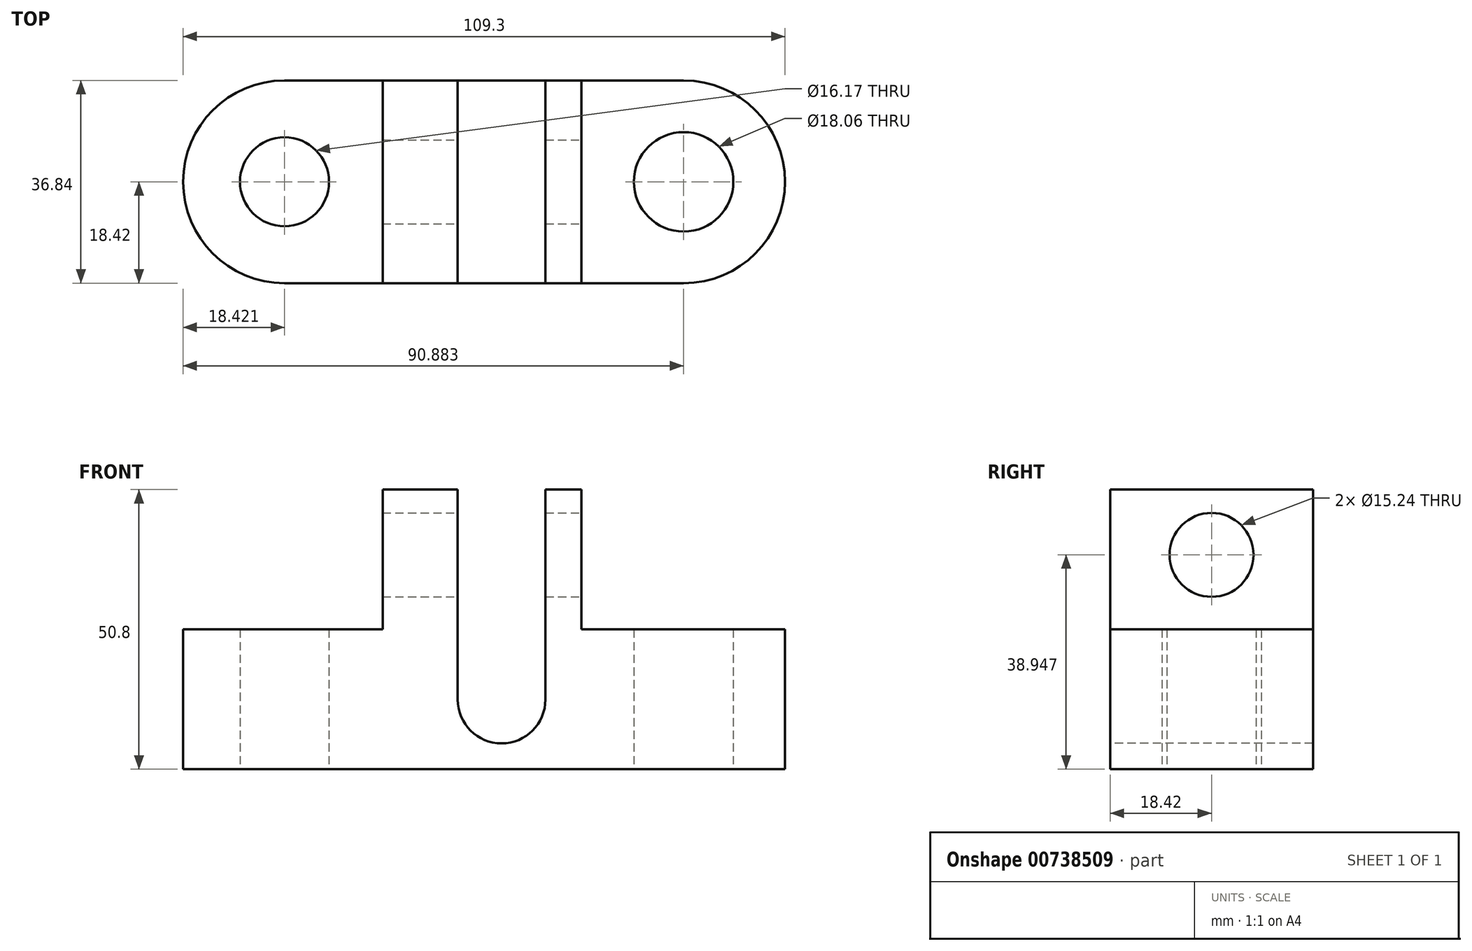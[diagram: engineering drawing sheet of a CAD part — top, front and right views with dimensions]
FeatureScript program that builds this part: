
annotation { "Feature Type Name" : "Feature", "Feature Type Description" : "" }
export const myFeature = defineFeature(function(context is Context, id is Id, definition is map)
    precondition{}
    {
        {
            var Q0;
            Q0=qCreatedBy(makeId("Top.planeOp"),FACE);
            var sketch = newSketch(context, id + "F0", { "sketchPlane" : qUnion([Q0])});
            skArc(sketch, "E0", {"start": v(-39.4, 18.42) * mm, "mid": v(-57.83, 0) * mm, "end": v(-39.4, -18.42) * mm});
            skArc(sketch, "E1", {"start": v(33.05, -18.42) * mm, "mid": v(51.47, 0) * mm, "end": v(33.05, 18.42) * mm});
            skLineSegment(sketch, "E2", {"start": v(-39.4, 18.42) * mm, "end": v(33.05, 18.42) * mm});
            skLineSegment(sketch, "E3", {"start": v(-39.4, -18.42) * mm, "end": v(33.05, -18.42) * mm});
            skCircle(sketch, "E4", {"center": v(-39.4, 0) * mm, "radius": 8.08 * mm});
            skCircle(sketch, "E5", {"center": v(33.05, 0) * mm, "radius": 9.03 * mm});
            skSolve(sketch);
        }
        {
            var Q0;
            Q0=makeQuery(id+"F0.imprint","IMPRINT",FACE,{"disambiguationData":[TD([[makeQuery(id+"F0.imprint","IMPRINT",EDGE,{"derivedFrom":sQuery(id+"F0.wireOp",EDGE,"E0")}),1.0]])]});
            extrude(context, id + "F1", {"entities" : qUnion([Q0]), "depth" : 25.4 * mm, "offsetDistance" : 25.4 * mm});
        }
        {
            var Q0;
            Q0=makeQuery(id+"F1.opExtrude","CAP_FACE",FACE,{"disambiguationData":[OSD([sQuery(id+"F0.wireOp",EDGE,"E0"),sQuery(id+"F0.wireOp",EDGE,"E1"),sQuery(id+"F0.wireOp",EDGE,"E2"),sQuery(id+"F0.wireOp",EDGE,"E3"),sQuery(id+"F0.wireOp",EDGE,"E4"),sQuery(id+"F0.wireOp",EDGE,"E5")])],"isStart":false});
            var sketch = newSketch(context, id + "F2", { "sketchPlane" : qUnion([Q0])});
            skLineSegment(sketch, "E6.bottom", {"start": v(-21.6, -18.42) * mm, "end": v(14.48, -18.42) * mm});
            skLineSegment(sketch, "E6.top", {"start": v(-21.6, 18.42) * mm, "end": v(14.48, 18.42) * mm});
            skLineSegment(sketch, "E6.left", {"start": v(-21.6, -18.42) * mm, "end": v(-21.6, 18.42) * mm});
            skLineSegment(sketch, "E6.right", {"start": v(14.48, -18.42) * mm, "end": v(14.48, 18.42) * mm});
            skSolve(sketch);
        }
        {
            var Q0;
            Q0=makeQuery(id+"F2.imprint","IMPRINT",FACE,{"disambiguationData":[TD([[makeQuery(id+"F2.imprint","IMPRINT",EDGE,{"derivedFrom":sQuery(id+"F2.wireOp",EDGE,"E6.bottom")}),1.0]])]});
            extrude(context, id + "F3", {"entities" : qUnion([Q0]), "operationType" : NewBodyOperationType.ADD, "depth" : 25.4 * mm, "offsetDistance" : 25.4 * mm});
        }
        {
            var Q0;
            Q0=makeQuery(id+"F3.boolean.opBoolean","MERGE",FACE,{"derivedFrom":[makeQuery(id+"F1.opExtrude","SWEPT_FACE",FACE,{"disambiguationData":[OSD([sQuery(id+"F0.wireOp",EDGE,"E3")])]}),makeQuery(id+"F3.opExtrude","SWEPT_FACE",FACE,{"disambiguationData":[OSD([sQuery(id+"F2.wireOp",EDGE,"E6.bottom")])]})]});
            var sketch = newSketch(context, id + "F4", { "sketchPlane" : qUnion([Q0])});
            skArc(sketch, "E7", {"start": v(-7.96, 12.65) * mm, "mid": v(0, 4.7) * mm, "end": v(7.96, 12.65) * mm});
            skLineSegment(sketch, "E8", {"start": v(-7.96, 12.65) * mm, "end": v(-7.96, 50.8) * mm});
            skLineSegment(sketch, "E9", {"start": v(7.96, 12.65) * mm, "end": v(7.96, 50.8) * mm});
            skLineSegment(sketch, "E10", {"start": v(-7.96, 50.8) * mm, "end": v(7.96, 50.8) * mm});
            skSolve(sketch);
        }
        {
            var Q0;
            Q0=makeQuery(id+"F4.imprint","IMPRINT",FACE,{"disambiguationData":[TD([[makeQuery(id+"F4.imprint","IMPRINT",EDGE,{"derivedFrom":sQuery(id+"F4.wireOp",EDGE,"E7")}),1.0]])]});
            extrude(context, id + "F5", {"entities" : qUnion([Q0]), "operationType" : NewBodyOperationType.REMOVE, "endBound" : BoundingType.THROUGH_ALL, "oppositeDirection" : true, "depth" : 25.4 * mm, "offsetDistance" : 25.4 * mm});
        }
        {
            var Q0;
            Q0=makeQuery(id+"F3.opExtrude","SWEPT_FACE",FACE,{"disambiguationData":[OSD([sQuery(id+"F2.wireOp",EDGE,"E6.right")])]});
            var sketch = newSketch(context, id + "F6", { "sketchPlane" : qUnion([Q0])});
            skCircle(sketch, "E11", {"center": v(0, 38.95) * mm, "radius": 7.62 * mm});
            skSolve(sketch);
        }
        {
            var Q0;
            Q0=makeQuery(id+"F6.imprint","IMPRINT",FACE,{"disambiguationData":[TD([[makeQuery(id+"F6.imprint","IMPRINT",EDGE,{"derivedFrom":sQuery(id+"F6.wireOp",EDGE,"E11")}),1.0]])]});
            extrude(context, id + "F7", {"entities" : qUnion([Q0]), "operationType" : NewBodyOperationType.REMOVE, "endBound" : BoundingType.THROUGH_ALL, "oppositeDirection" : true, "depth" : 25.4 * mm, "offsetDistance" : 25.4 * mm});
        }
    });
